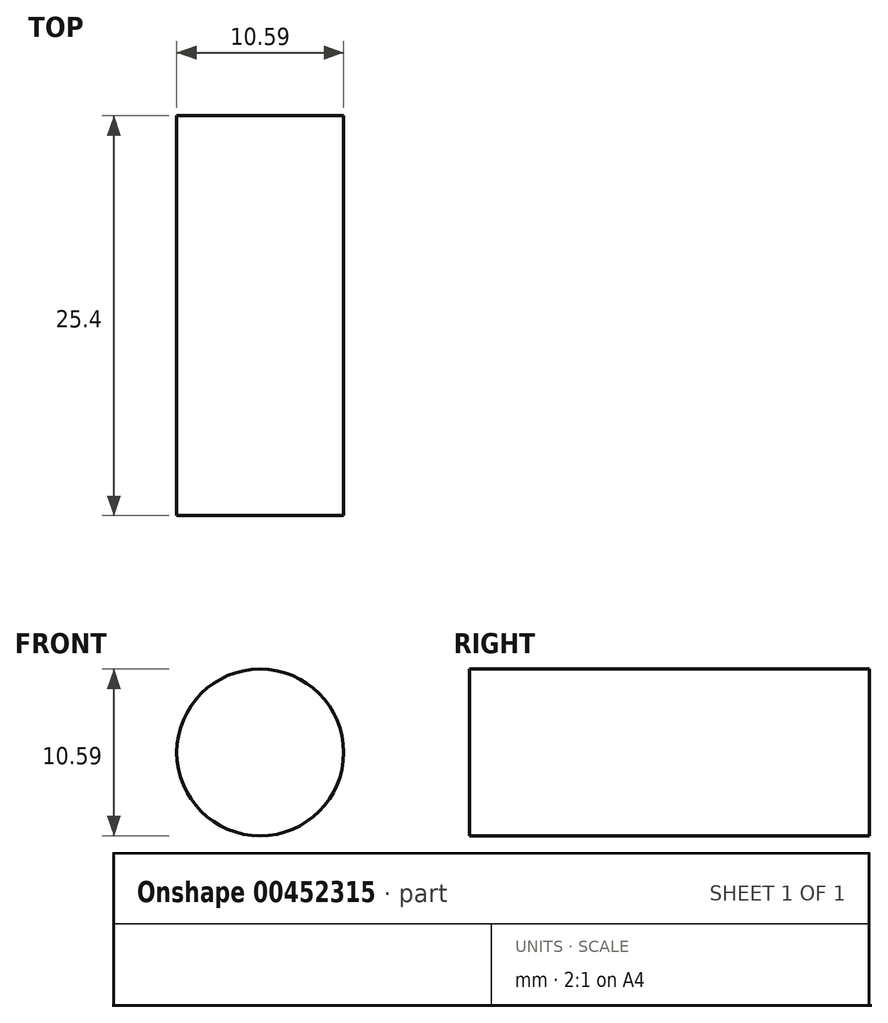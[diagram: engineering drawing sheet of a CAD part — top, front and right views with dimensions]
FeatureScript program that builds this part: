
annotation { "Feature Type Name" : "Feature", "Feature Type Description" : "" }
export const myFeature = defineFeature(function(context is Context, id is Id, definition is map)
    precondition{}
    {
        {
            var Q0;
            Q0=qCreatedBy(makeId("Front.planeOp"),FACE);
            var sketch = newSketch(context, id + "F0", { "sketchPlane" : qUnion([Q0])});
            skCircle(sketch, "E0", {"center": v(2.56, -4.64) * mm, "radius": 5.3 * mm});
            skSolve(sketch);
        }
        {
            var Q0;
            Q0 = qSketchRegion(id + "F0", true);
            extrude(context, id + "F1", {"entities" : qUnion([Q0]), "depth" : 25.4 * mm});
        }
    });
